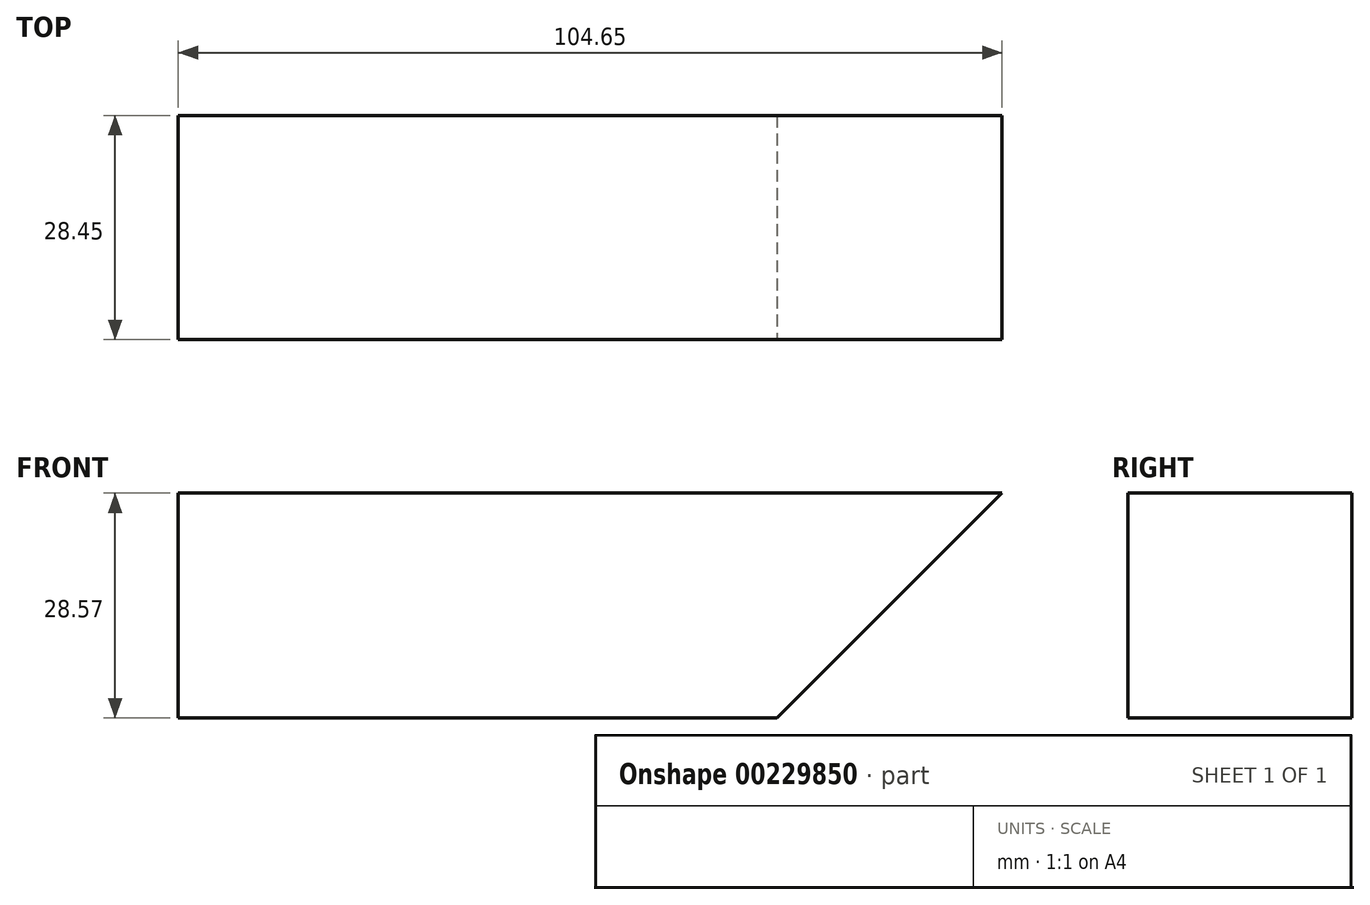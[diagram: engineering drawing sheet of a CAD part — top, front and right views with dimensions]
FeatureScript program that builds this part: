
annotation { "Feature Type Name" : "Feature", "Feature Type Description" : "" }
export const myFeature = defineFeature(function(context is Context, id is Id, definition is map)
    precondition{}
    {
        {
            var Q0;
            Q0=qCreatedBy(makeId("Top.planeOp"),FACE);
            var sketch = newSketch(context, id + "F0", { "sketchPlane" : qUnion([Q0])});
            skLineSegment(sketch, "E0.bottom", {"start": v(-78, 11.13) * mm, "end": v(26.65, 11.13) * mm});
            skLineSegment(sketch, "E0.top", {"start": v(-78, -17.32) * mm, "end": v(26.65, -17.32) * mm});
            skLineSegment(sketch, "E0.left", {"start": v(-78, 11.13) * mm, "end": v(-78, -17.32) * mm});
            skLineSegment(sketch, "E0.right", {"start": v(26.65, 11.13) * mm, "end": v(26.65, -17.32) * mm});
            skSolve(sketch);
        }
        {
            var Q0;
            Q0 = qSketchRegion(id + "F0", true);
            extrude(context, id + "F1", {"entities" : qUnion([Q0]), "depth" : 28.57 * mm});
        }
        {
            var Q0;
            Q0=makeQuery(id+"F1.opExtrude","CAP_EDGE",EDGE,{"disambiguationData":[OSD([sQuery(id+"F0.wireOp",EDGE,"E0.right")])],"isStart":true});
            chamfer(context, id + "F2", {"entities" : qUnion([Q0]), "chamferType" : ChamferType.OFFSET_ANGLE, "width" : 28.57 * mm, "oppositeDirection" : false, "angle" : 45 * degree, "tangentPropagation" : true});
        }
    });
